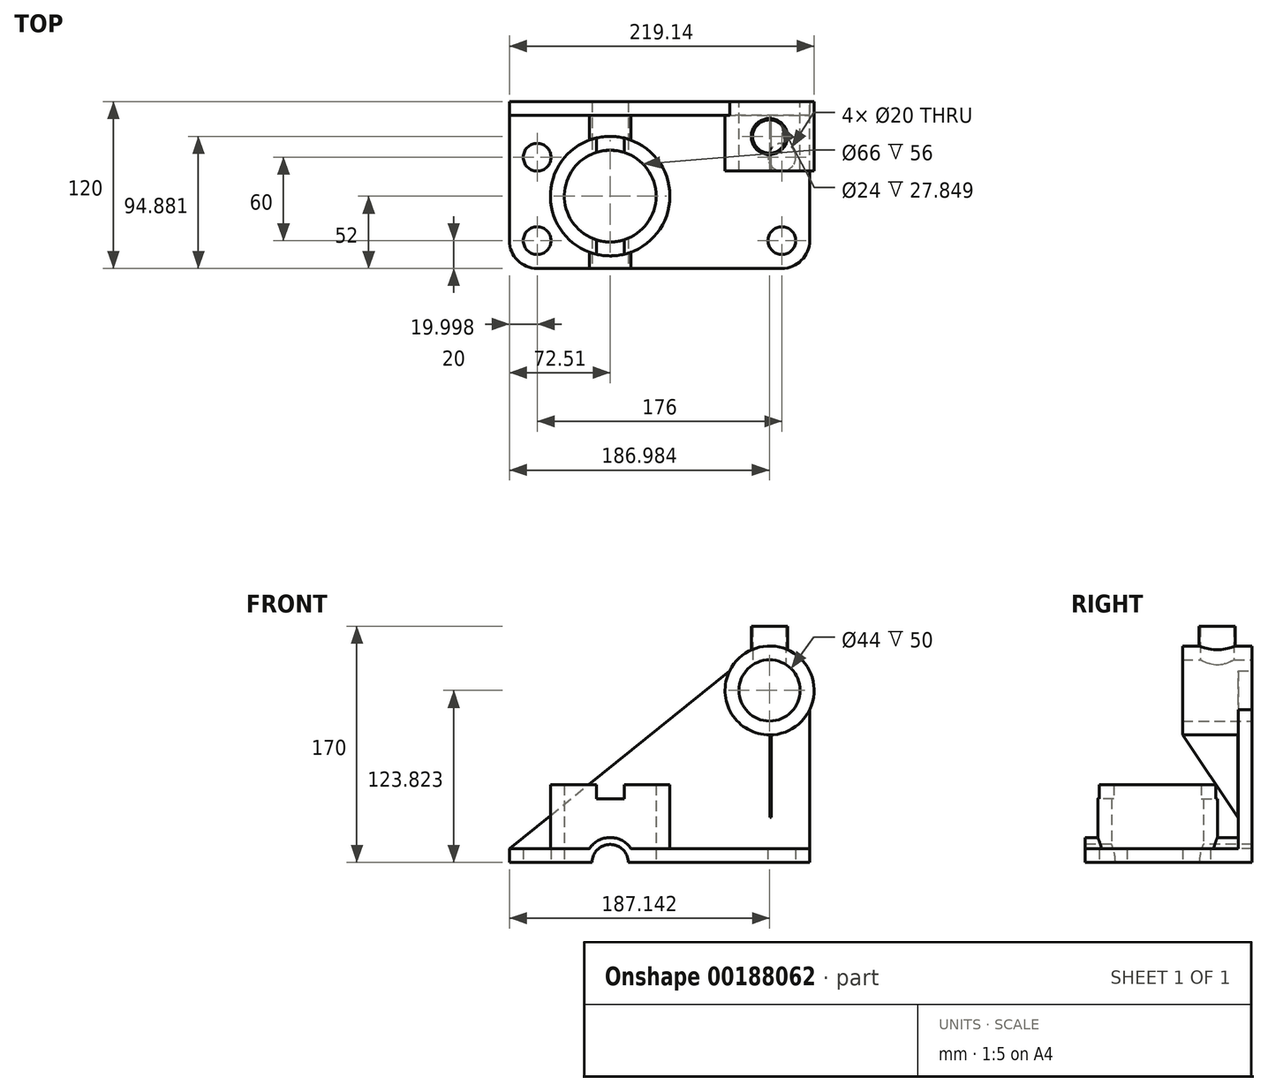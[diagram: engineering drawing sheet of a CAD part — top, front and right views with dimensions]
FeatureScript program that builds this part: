
annotation { "Feature Type Name" : "Feature", "Feature Type Description" : "" }
export const myFeature = defineFeature(function(context is Context, id is Id, definition is map)
    precondition{}
    {
        {
            var Q0;
            Q0=qCreatedBy(makeId("Top.planeOp"),FACE);
            var sketch = newSketch(context, id + "F0", { "sketchPlane" : qUnion([Q0])});
            skCircle(sketch, "E0", {"center": v(0, 0) * mm, "radius": 33 * mm});
            skLineSegment(sketch, "E1", {"start": v(-72.51, 68) * mm, "end": v(-72.51, -32) * mm});
            skPoint(sketch, "E2", {"position": v(-72.51, 8) * mm});
            skLineSegment(sketch, "E3", {"start": v(-72.51, 68) * mm, "end": v(143.49, 68) * mm});
            skLineSegment(sketch, "E4", {"start": v(-52.51, -52) * mm, "end": v(123.49, -52) * mm});
            skPoint(sketch, "E5.visualSharp", {"position": v(-72.51, -52) * mm});
            skArc(sketch, "E5.filletArc", {"start": v(-72.51, -32) * mm, "mid": v(-66.65, -46.14) * mm, "end": v(-52.51, -52) * mm});
            skCircle(sketch, "E6", {"center": v(-52.51, -32) * mm, "radius": 10 * mm});
            skCircle(sketch, "E7", {"center": v(-52.51, 28) * mm, "radius": 10 * mm});
            skCircle(sketch, "E8", {"center": v(0, 0) * mm, "radius": 43 * mm});
            skLineSegment(sketch, "E9", {"start": v(-52.51, 28) * mm, "end": v(-72.51, 28) * mm, "construction": true});
            skLineSegment(sketch, "E10", {"start": v(143.49, 68) * mm, "end": v(143.49, -32) * mm});
            skCircle(sketch, "E11", {"center": v(123.49, -32) * mm, "radius": 10 * mm});
            skPoint(sketch, "E12.visualSharp", {"position": v(143.49, -52) * mm});
            skArc(sketch, "E12.filletArc", {"start": v(123.49, -52) * mm, "mid": v(137.63, -46.14) * mm, "end": v(143.49, -32) * mm});
            skLineSegment(sketch, "E13", {"start": v(-52.51, -52) * mm, "end": v(-72.51, -52) * mm, "construction": true});
            skLineSegment(sketch, "E14", {"start": v(-72.51, -32) * mm, "end": v(-72.51, -52) * mm, "construction": true});
            skLineSegment(sketch, "E15", {"start": v(-72.51, 58) * mm, "end": v(143.49, 58) * mm});
            skLineSegment(sketch, "E16", {"start": v(-52.51, -32) * mm, "end": v(123.49, -32) * mm, "construction": true});
            skCircle(sketch, "E17", {"center": v(123.49, 28) * mm, "radius": 10 * mm});
            skLineSegment(sketch, "E18", {"start": v(59.26, 0) * mm, "end": v(59.26, -32) * mm, "construction": true});
            skLineSegment(sketch, "E19", {"start": v(-52.51, 28) * mm, "end": v(123.49, 28) * mm, "construction": true});
            skLineSegment(sketch, "E20", {"start": v(0, 33) * mm, "end": v(0, 22.46) * mm, "construction": true});
            skLineSegment(sketch, "E21", {"start": v(0, 22.46) * mm, "end": v(-10, 22.46) * mm, "construction": true});
            skLineSegment(sketch, "E22", {"start": v(0, 22.46) * mm, "end": v(10, 22.46) * mm, "construction": true});
            skLineSegment(sketch, "E23", {"start": v(10, 31.45) * mm, "end": v(10, 41.82) * mm});
            skLineSegment(sketch, "E24", {"start": v(-10, 31.45) * mm, "end": v(-10, 41.82) * mm});
            skLineSegment(sketch, "E25", {"start": v(-10, -31.45) * mm, "end": v(-10, -41.82) * mm});
            skLineSegment(sketch, "E26", {"start": v(10, -31.45) * mm, "end": v(10, -41.82) * mm});
            skSolve(sketch);
        }
        {
            var Q0;
            Q0 = qSketchRegion(id + "F0", true);
            extrude(context, id + "F1", {"entities" : qUnion([Q0]), "depth" : 10 * mm});
        }
        {
            var Q0;
            {var subQ0=sQuery(id+"F0.wireOp",EDGE,"E24");Q0=makeQuery(id+"F0.imprint","IMPRINT",FACE,{"disambiguationData":[TD([[makeQuery(id+"F0.imprint","IMPRINT",EDGE,{"derivedFrom":subQ0}),1.0]])]});}
            var Q1;
            {var subQ0=sQuery(id+"F0.wireOp",EDGE,"E23");Q1=makeQuery(id+"F0.imprint","IMPRINT",FACE,{"disambiguationData":[TD([[makeQuery(id+"F0.imprint","IMPRINT",EDGE,{"derivedFrom":subQ0}),-1.0]])]});}
            extrude(context, id + "F2", {"entities" : qUnion([Q0, Q1]), "operationType" : NewBodyOperationType.ADD, "depth" : 56 * mm});
        }
        {
            var Q0;
            {var subQ0=sQuery(id+"F0.wireOp",EDGE,"E23");Q0=makeQuery(id+"F0.imprint","IMPRINT",FACE,{"disambiguationData":[TD([[makeQuery(id+"F0.imprint","IMPRINT",EDGE,{"derivedFrom":subQ0}),1.0]])]});}
            var Q1;
            {var subQ0=sQuery(id+"F0.wireOp",EDGE,"E25");Q1=makeQuery(id+"F0.imprint","IMPRINT",FACE,{"disambiguationData":[TD([[makeQuery(id+"F0.imprint","IMPRINT",EDGE,{"derivedFrom":subQ0}),1.0]])]});}
            extrude(context, id + "F3", {"entities" : qUnion([Q0, Q1]), "operationType" : NewBodyOperationType.ADD, "depth" : 46 * mm});
        }
        {
            var Q0;
            Q0=qCreatedBy(makeId("Front.planeOp"),FACE);
            var sketch = newSketch(context, id + "F4", { "sketchPlane" : qUnion([Q0])});
            skCircle(sketch, "E27", {"center": v(0, 0) * mm, "radius": 13 * mm});
            skCircle(sketch, "E28", {"center": v(0, 0) * mm, "radius": 18 * mm});
            skSolve(sketch);
        }
        {
            var Q0;
            Q0=makeQuery(id+"F4.imprint","IMPRINT",FACE,{"disambiguationData":[TD([[makeQuery(id+"F4.imprint","IMPRINT",EDGE,{"derivedFrom":sQuery(id+"F4.wireOp",EDGE,"E27")}),1.0]])]});
            extrude(context, id + "F5", {"entities" : qUnion([Q0]), "operationType" : NewBodyOperationType.REMOVE, "oppositeDirection" : true, "depth" : 100 * mm});
        }
        {
            var Q0;
            Q0=makeQuery(id+"F4.imprint","IMPRINT",FACE,{"disambiguationData":[TD([[makeQuery(id+"F4.imprint","IMPRINT",EDGE,{"derivedFrom":sQuery(id+"F4.wireOp",EDGE,"E27")}),1.0]])]});
            extrude(context, id + "F6", {"entities" : qUnion([Q0]), "operationType" : NewBodyOperationType.REMOVE, "depth" : 100 * mm});
        }
        {
            var Q0;
            Q0=makeQuery(id+"F4.imprint","IMPRINT",FACE,{"disambiguationData":[TD([[makeQuery(id+"F4.imprint","IMPRINT",EDGE,{"derivedFrom":sQuery(id+"F4.wireOp",EDGE,"E27")}),-1.0]])]});
            extrude(context, id + "F7", {"entities" : qUnion([Q0]), "operationType" : NewBodyOperationType.ADD, "depth" : 52 * mm});
        }
        {
            var Q0;
            Q0=makeQuery(id+"F4.imprint","IMPRINT",FACE,{"disambiguationData":[TD([[makeQuery(id+"F4.imprint","IMPRINT",EDGE,{"derivedFrom":sQuery(id+"F4.wireOp",EDGE,"E27")}),-1.0]])]});
            extrude(context, id + "F8", {"entities" : qUnion([Q0]), "operationType" : NewBodyOperationType.ADD, "oppositeDirection" : true, "depth" : 68 * mm});
        }
        {
            var Q0;
            Q0=qCreatedBy(makeId("Top.planeOp"),FACE);
            cPlane(context, id + "F9", {"entities" : qUnion([Q0]), "cplaneType" : CPlaneType.OFFSET, "offset" : 60 * mm, "width" : 150 * mm, "height" : 150 * mm});
        }
        {
            var Q0;
            Q0=qCreatedBy(id+"F9.planeOp",FACE);
            var sketch = newSketch(context, id + "F10", { "sketchPlane" : qUnion([Q0])});
            skCircle(sketch, "E29", {"center": v(0, 0) * mm, "radius": 33 * mm});
            skSolve(sketch);
        }
        {
            var Q0;
            Q0=makeQuery(id+"F10.imprint","IMPRINT",FACE,{"disambiguationData":[TD([[makeQuery(id+"F10.imprint","IMPRINT",EDGE,{"derivedFrom":sQuery(id+"F10.wireOp",EDGE,"E29")}),1.0]])]});
            extrude(context, id + "F11", {"entities" : qUnion([Q0]), "operationType" : NewBodyOperationType.REMOVE, "oppositeDirection" : true, "depth" : 100 * mm});
        }
        {
            var Q0;
            Q0=qCreatedBy(makeId("Front.planeOp"),FACE);
            cPlane(context, id + "F12", {"entities" : qUnion([Q0]), "cplaneType" : CPlaneType.OFFSET, "offset" : 60 * mm, "width" : 150 * mm, "height" : 150 * mm});
        }
        {
            var Q0;
            Q0=qCreatedBy(id+"F12.planeOp",FACE);
            var sketch = newSketch(context, id + "F13", { "sketchPlane" : qUnion([Q0])});
            skLineSegment(sketch, "E30.bottom", {"start": v(-20.37, 0) * mm, "end": v(20.73, 0) * mm});
            skLineSegment(sketch, "E30.top", {"start": v(-20.37, -21.22) * mm, "end": v(20.73, -21.22) * mm});
            skLineSegment(sketch, "E30.left", {"start": v(-20.37, 0) * mm, "end": v(-20.37, -21.22) * mm});
            skLineSegment(sketch, "E30.right", {"start": v(20.73, 0) * mm, "end": v(20.73, -21.22) * mm});
            skSolve(sketch);
        }
        {
            var Q0;
            Q0=makeQuery(id+"F13.imprint","IMPRINT",FACE,{"disambiguationData":[TD([[makeQuery(id+"F13.imprint","IMPRINT",EDGE,{"derivedFrom":sQuery(id+"F13.wireOp",EDGE,"E30.bottom")}),-1.0]])]});
            extrude(context, id + "F14", {"entities" : qUnion([Q0]), "operationType" : NewBodyOperationType.REMOVE, "oppositeDirection" : true, "depth" : 150 * mm});
        }
        {
            var Q0;
            Q0=qCreatedBy(makeId("Front.planeOp"),FACE);
            cPlane(context, id + "F15", {"entities" : qUnion([Q0]), "cplaneType" : CPlaneType.OFFSET, "offset" : 68 * mm, "oppositeDirection" : true, "width" : 150 * mm, "height" : 150 * mm});
        }
        {
            var Q0;
            Q0=qCreatedBy(id+"F15.planeOp",FACE);
            var sketch = newSketch(context, id + "F16", { "sketchPlane" : qUnion([Q0])});
            skPoint(sketch, "E31", {"position": v(143.49, 10) * mm});
            skPoint(sketch, "E32", {"position": v(-58.94, 10) * mm});
            skLineSegment(sketch, "E33", {"start": v(143.49, 10) * mm, "end": v(-58.94, 10) * mm});
            skLineSegment(sketch, "E34", {"start": v(143.49, 10) * mm, "end": v(143.49, 109.99) * mm});
            skLineSegment(sketch, "E35", {"start": v(-58.94, 10) * mm, "end": v(-72.51, 10) * mm});
            skLineSegment(sketch, "E36", {"start": v(-72.51, 10) * mm, "end": v(85.96, 138.03) * mm});
            skLineSegment(sketch, "E37", {"start": v(189.83, 10) * mm, "end": v(189.83, 100) * mm, "construction": true});
            skLineSegment(sketch, "E38", {"start": v(-72.51, 156) * mm, "end": v(143.49, 10) * mm, "construction": true});
            skLineSegment(sketch, "E39", {"start": v(35.49, 156) * mm, "end": v(35.49, 83) * mm, "construction": true});
            skPoint(sketch, "E40", {"position": v(116.49, 119.5) * mm});
            skLineSegment(sketch, "E41", {"start": v(143.49, 10) * mm, "end": v(143.49, 109.99) * mm, "construction": true});
            skCircle(sketch, "E42", {"center": v(114.63, 123.82) * mm, "radius": 32 * mm});
            skCircle(sketch, "E43", {"center": v(114.63, 123.82) * mm, "radius": 22 * mm});
            skSolve(sketch);
        }
        {
            var Q0;
            Q0=makeQuery(id+"F16.imprint","IMPRINT",FACE,{"disambiguationData":[TD([[makeQuery(id+"F16.imprint","IMPRINT",EDGE,{"derivedFrom":sQuery(id+"F16.wireOp",EDGE,"E33")}),-1.0]])]});
            extrude(context, id + "F17", {"entities" : qUnion([Q0]), "operationType" : NewBodyOperationType.ADD, "depth" : 10 * mm});
        }
        {
            var Q0;
            Q0=qCreatedBy(id+"F15.planeOp",FACE);
            var sketch = newSketch(context, id + "F18", { "sketchPlane" : qUnion([Q0])});
            skCircle(sketch, "E44", {"center": v(0, 0) * mm, "radius": 13 * mm});
            skSolve(sketch);
        }
        {
            var Q0;
            Q0=makeQuery(id+"F18.imprint","IMPRINT",FACE,{"disambiguationData":[TD([[makeQuery(id+"F18.imprint","IMPRINT",EDGE,{"derivedFrom":sQuery(id+"F18.wireOp",EDGE,"E44")}),1.0]])]});
            extrude(context, id + "F19", {"entities" : qUnion([Q0]), "operationType" : NewBodyOperationType.REMOVE, "depth" : 20 * mm});
        }
        {
            var Q0;
            {var subQ0=sQuery(id+"F16.wireOp",EDGE,"E42");var subQ1=makeQuery(id+"F16.imprint","INTERSECT",VERTEX,{"derivedFrom":[sQuery(id+"F16.wireOp",EDGE,"E34"),subQ0]});Q0=makeQuery(id+"F16.imprint","IMPRINT",FACE,{"disambiguationData":[TD([[makeQuery(id+"F16.imprint","IMPRINT",EDGE,{"disambiguationData":[TD([[subQ1,1.0]])],"derivedFrom":subQ0}),1.0]])]});}
            extrude(context, id + "F20", {"entities" : qUnion([Q0]), "operationType" : NewBodyOperationType.ADD, "depth" : 50 * mm});
        }
        {
            var Q0;
            Q0=qCreatedBy(id+"F9.planeOp",FACE);
            cPlane(context, id + "F21", {"entities" : qUnion([Q0]), "cplaneType" : CPlaneType.OFFSET, "offset" : 70 * mm, "width" : 150 * mm, "height" : 150 * mm});
        }
        {
            var Q0;
            Q0=qCreatedBy(id+"F21.planeOp",FACE);
            var sketch = newSketch(context, id + "F22", { "sketchPlane" : qUnion([Q0])});
            skPoint(sketch, "E45", {"position": v(114.47, 42.88) * mm});
            skCircle(sketch, "E46", {"center": v(114.47, 42.88) * mm, "radius": 13 * mm});
            skCircle(sketch, "E47", {"center": v(114.47, 42.88) * mm, "radius": 12 * mm});
            skSolve(sketch);
        }
        {
            var Q0;
            Q0=makeQuery(id+"F22.imprint","IMPRINT",FACE,{"disambiguationData":[TD([[makeQuery(id+"F22.imprint","IMPRINT",EDGE,{"derivedFrom":sQuery(id+"F22.wireOp",EDGE,"E46")}),1.0]])]});
            extrude(context, id + "F23", {"entities" : qUnion([Q0]), "operationType" : NewBodyOperationType.ADD, "depth" : 40 * mm});
        }
        {
            var Q0;
            Q0=makeQuery(id+"F16.imprint","IMPRINT",FACE,{"disambiguationData":[TD([[makeQuery(id+"F16.imprint","IMPRINT",EDGE,{"derivedFrom":sQuery(id+"F16.wireOp",EDGE,"E43")}),1.0]])]});
            extrude(context, id + "F24", {"entities" : qUnion([Q0]), "operationType" : NewBodyOperationType.REMOVE, "depth" : 30 * mm});
        }
        {
            var Q0;
            Q0=makeQuery(id+"F16.imprint","IMPRINT",FACE,{"disambiguationData":[TD([[makeQuery(id+"F16.imprint","IMPRINT",EDGE,{"derivedFrom":sQuery(id+"F16.wireOp",EDGE,"E43")}),1.0]])]});
            extrude(context, id + "F25", {"entities" : qUnion([Q0]), "operationType" : NewBodyOperationType.REMOVE, "depth" : 60 * mm});
        }
        {
            var Q0;
            Q0=makeQuery(id+"F22.imprint","IMPRINT",FACE,{"disambiguationData":[TD([[makeQuery(id+"F22.imprint","IMPRINT",EDGE,{"derivedFrom":sQuery(id+"F22.wireOp",EDGE,"E47")}),1.0]])]});
            extrude(context, id + "F26", {"entities" : qUnion([Q0]), "operationType" : NewBodyOperationType.REMOVE, "depth" : 30 * mm});
        }
        {
            var Q0;
            Q0=qCreatedBy(makeId("Right.planeOp"),FACE);
            cPlane(context, id + "F27", {"entities" : qUnion([Q0]), "cplaneType" : CPlaneType.OFFSET, "offset" : 115 * mm, "width" : 150 * mm, "height" : 150 * mm});
        }
        {
            var Q0;
            Q0=qCreatedBy(id+"F27.planeOp",FACE);
            var sketch = newSketch(context, id + "F28", { "sketchPlane" : qUnion([Q0])});
            skLineSegment(sketch, "E48", {"start": v(18, 91.82) * mm, "end": v(57.84, 32.64) * mm});
            skLineSegment(sketch, "E49", {"start": v(57.84, 32.64) * mm, "end": v(57.84, 92.09) * mm});
            skLineSegment(sketch, "E50", {"start": v(57.84, 92.09) * mm, "end": v(18, 91.82) * mm});
            skSolve(sketch);
        }
        {
            var Q0;
            Q0=makeQuery(id+"F28.imprint","IMPRINT",FACE,{"disambiguationData":[TD([[makeQuery(id+"F28.imprint","IMPRINT",EDGE,{"derivedFrom":sQuery(id+"F28.wireOp",EDGE,"E48")}),1.0]])]});
            extrude(context, id + "F29", {"entities" : qUnion([Q0]), "operationType" : NewBodyOperationType.ADD, "depth" : 1 * mm});
        }
    });
